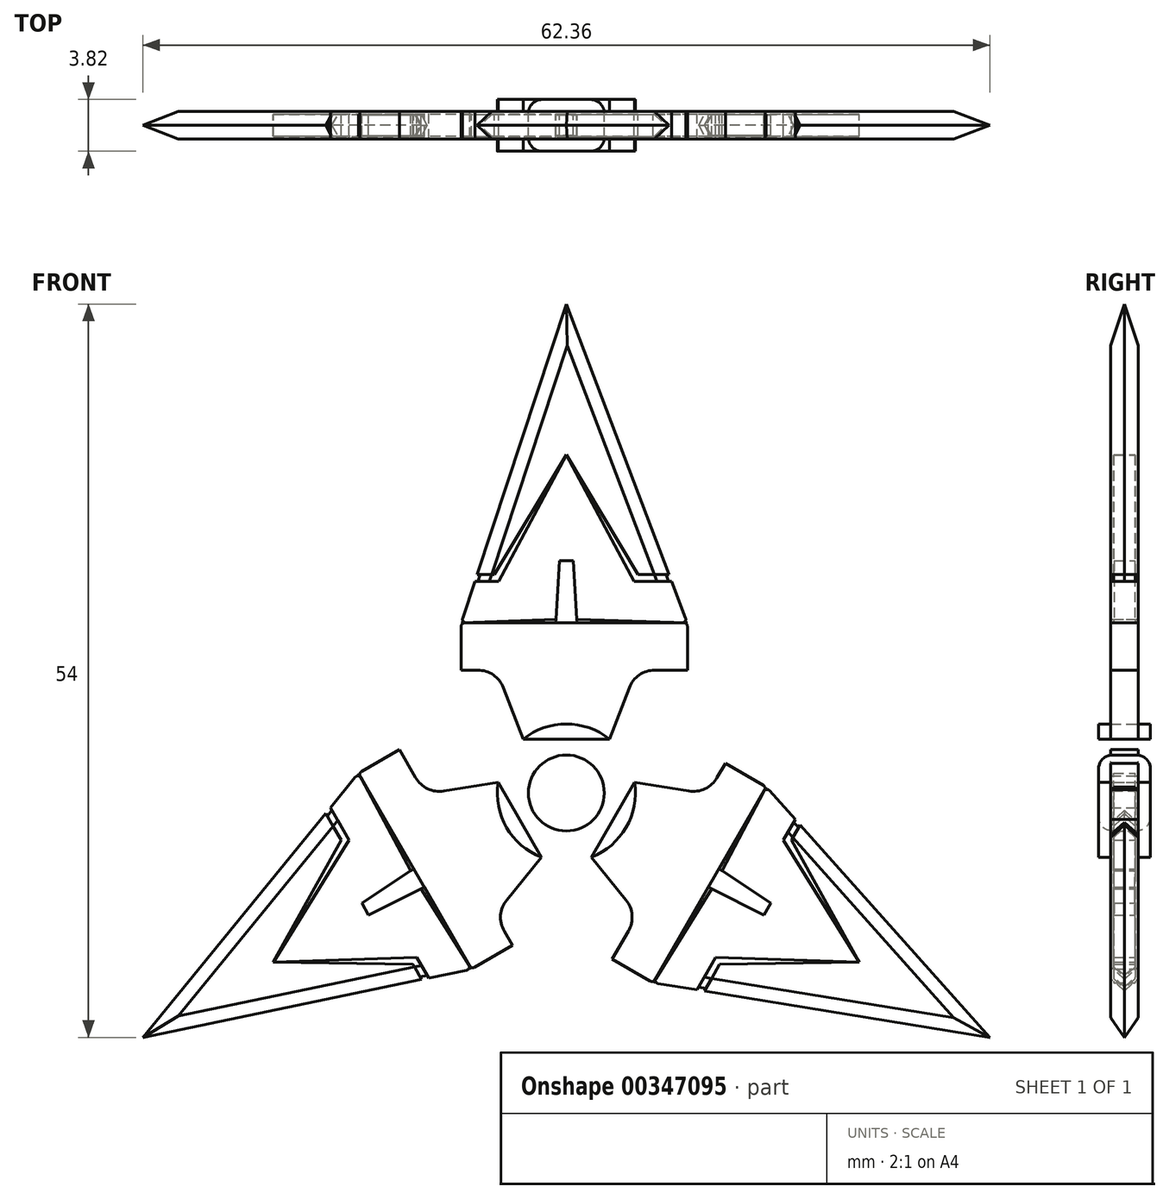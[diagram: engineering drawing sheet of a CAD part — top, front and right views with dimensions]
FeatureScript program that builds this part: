
annotation { "Feature Type Name" : "Feature", "Feature Type Description" : "" }
export const myFeature = defineFeature(function(context is Context, id is Id, definition is map)
    precondition{}
    {
        {
            var Q0;
            Q0=qCreatedBy(makeId("Front.planeOp"),FACE);
            var sketch = newSketch(context, id + "F0", { "sketchPlane" : qUnion([Q0])});
            skCircle(sketch, "E0", {"center": v(0, 0) * mm, "radius": 5.08 * mm});
            skLineSegment(sketch, "E1.bottom", {"start": v(-7.75, 12.52) * mm, "end": v(8.91, 12.52) * mm});
            skLineSegment(sketch, "E1.top", {"start": v(-7.75, 9.04) * mm, "end": v(8.91, 9.04) * mm});
            skLineSegment(sketch, "E1.left", {"start": v(-7.75, 12.52) * mm, "end": v(-7.75, 9.04) * mm});
            skLineSegment(sketch, "E1.right", {"start": v(8.91, 12.52) * mm, "end": v(8.91, 9.04) * mm});
            skLineSegment(sketch, "E2.right", {"start": v(3.18, 9.04) * mm, "end": v(3.18, 3.96) * mm});
            skLineSegment(sketch, "E3.MirrorCS", {"start": v(-3.18, 9.04) * mm, "end": v(-3.18, 3.96) * mm});
            skLineSegment(sketch, "E4", {"start": v(-3.18, 3.96) * mm, "end": v(-5.13, 9.04) * mm});
            skLineSegment(sketch, "E5", {"start": v(3.18, 3.96) * mm, "end": v(5.13, 9.04) * mm});
            skLineSegment(sketch, "E6", {"start": v(-7.75, 12.52) * mm, "end": v(0, 36) * mm});
            skLineSegment(sketch, "E7", {"start": v(8.91, 12.52) * mm, "end": v(0, 36) * mm});
            skLineSegment(sketch, "E8", {"start": v(0, 36) * mm, "end": v(0, 0) * mm});
            skCircle(sketch, "E9.0", {"center": v(0, 0) * mm, "radius": 2.8 * mm});
            skLineSegment(sketch, "E10", {"start": v(-3.18, 3.96) * mm, "end": v(3.18, 3.96) * mm});
            skLineSegment(sketch, "E11.bottom", {"start": v(0.78, 12.52) * mm, "end": v(-0.78, 12.52) * mm});
            skLineSegment(sketch, "E11.top", {"start": v(0.5, 17.1) * mm, "end": v(-0.5, 17.1) * mm});
            skPoint(sketch, "E11.middle", {"position": v(0, 16.34) * mm});
            skLineSegment(sketch, "E12.MirrorCS", {"start": v(0, 24.88) * mm, "end": v(4.98, 15.58) * mm});
            skLineSegment(sketch, "E13.MirrorCS", {"start": v(4.98, 15.58) * mm, "end": v(7.75, 15.58) * mm});
            skLineSegment(sketch, "E14.0", {"start": v(5.29, 16.1) * mm, "end": v(7.56, 16.1) * mm});
            skLineSegment(sketch, "E15", {"start": v(5.29, 16.1) * mm, "end": v(0, 24.9) * mm});
            skLineSegment(sketch, "E16.MirrorCS", {"start": v(-5.29, 16.1) * mm, "end": v(0, 24.9) * mm});
            skLineSegment(sketch, "E17.MirrorCS", {"start": v(0, 24.88) * mm, "end": v(-4.98, 15.58) * mm});
            skLineSegment(sketch, "E18.MirrorCS", {"start": v(-5.29, 16.1) * mm, "end": v(-7.56, 16.1) * mm});
            skLineSegment(sketch, "E19.MirrorCS", {"start": v(-4.98, 15.58) * mm, "end": v(-7.75, 15.58) * mm});
            skLineSegment(sketch, "E20", {"start": v(-0.5, 17.1) * mm, "end": v(-0.78, 12.52) * mm});
            skLineSegment(sketch, "E21", {"start": v(0.5, 17.1) * mm, "end": v(0.78, 12.52) * mm});
            skLineSegment(sketch, "E22", {"start": v(-7.75, 12.52) * mm, "end": v(-0.77, 12.8) * mm});
            skLineSegment(sketch, "E23", {"start": v(0.77, 12.8) * mm, "end": v(8.91, 12.52) * mm});
            skLineSegment(sketch, "E24.1.0", {"start": v(-9.42, -1.77) * mm, "end": v(-5.02, 0.77) * mm});
            skPoint(sketch, "E24.1.1", {"position": v(-14.15, -8.17) * mm});
            skLineSegment(sketch, "E24.1.2", {"start": v(-15.3, 1.45) * mm, "end": v(-12.29, 3.2) * mm});
            skLineSegment(sketch, "E24.1.3", {"start": v(-6.97, -12.97) * mm, "end": v(-15.3, 1.45) * mm});
            skLineSegment(sketch, "E24.1.4", {"start": v(-16.58, -3.47) * mm, "end": v(-21.57, -12.45) * mm});
            skLineSegment(sketch, "E24.1.5", {"start": v(-3.96, -11.23) * mm, "end": v(-12.29, 3.2) * mm});
            skLineSegment(sketch, "E24.1.6", {"start": v(-21.55, -12.44) * mm, "end": v(-11, -12.1) * mm});
            skLineSegment(sketch, "E24.1.7", {"start": v(-11.3, -12.63) * mm, "end": v(-21.57, -12.45) * mm});
            skLineSegment(sketch, "E24.1.8", {"start": v(-1.85, -4.73) * mm, "end": v(-5.02, 0.77) * mm});
            skLineSegment(sketch, "E24.1.9", {"start": v(-11.46, -5.73) * mm, "end": v(-15.3, 1.45) * mm});
            skLineSegment(sketch, "E24.1.10", {"start": v(-5.02, 0.77) * mm, "end": v(-10.4, -0.08) * mm});
            skLineSegment(sketch, "E24.1.11", {"start": v(-6.97, -12.97) * mm, "end": v(-3.96, -11.23) * mm});
            skLineSegment(sketch, "E24.1.12", {"start": v(-6.24, -7.27) * mm, "end": v(-1.85, -4.73) * mm});
            skLineSegment(sketch, "E24.1.13", {"start": v(-6.97, -12.97) * mm, "end": v(-31.18, -18) * mm});
            skLineSegment(sketch, "E24.1.14", {"start": v(-6.97, -12.97) * mm, "end": v(-10.7, -7.06) * mm});
            skLineSegment(sketch, "E24.1.15", {"start": v(-1.85, -4.73) * mm, "end": v(-5.27, -8.96) * mm});
            skLineSegment(sketch, "E24.1.16", {"start": v(-21.55, -12.44) * mm, "end": v(-15.99, -3.47) * mm});
            skLineSegment(sketch, "E24.1.17", {"start": v(-15.3, 1.45) * mm, "end": v(-31.18, -18) * mm});
            skLineSegment(sketch, "E24.1.18", {"start": v(-15.06, -8.11) * mm, "end": v(-11.24, -5.58) * mm});
            skLineSegment(sketch, "E24.1.19", {"start": v(-14.55, -8.98) * mm, "end": v(-10.46, -6.94) * mm});
            skLineSegment(sketch, "E24.1.20", {"start": v(-15.06, -8.11) * mm, "end": v(-14.55, -8.98) * mm});
            skLineSegment(sketch, "E24.1.21", {"start": v(-16.58, -3.47) * mm, "end": v(-17.71, -1.5) * mm});
            skLineSegment(sketch, "E24.1.22", {"start": v(-11.24, -5.58) * mm, "end": v(-10.46, -6.94) * mm});
            skLineSegment(sketch, "E24.1.23", {"start": v(-11, -12.1) * mm, "end": v(-9.62, -14.5) * mm});
            skLineSegment(sketch, "E24.1.24", {"start": v(-15.99, -3.47) * mm, "end": v(-17.37, -1.08) * mm});
            skLineSegment(sketch, "E24.1.25", {"start": v(-11.3, -12.63) * mm, "end": v(-10.16, -14.6) * mm});
            skLineSegment(sketch, "E24.2.0", {"start": v(6.24, -7.27) * mm, "end": v(1.85, -4.73) * mm});
            skPoint(sketch, "E24.2.1", {"position": v(14.15, -8.17) * mm});
            skLineSegment(sketch, "E24.2.2", {"start": v(6.4, -13.98) * mm, "end": v(3.38, -12.24) * mm});
            skLineSegment(sketch, "E24.2.3", {"start": v(14.72, 0.45) * mm, "end": v(6.4, -13.98) * mm});
            skLineSegment(sketch, "E24.2.4", {"start": v(11.3, -12.63) * mm, "end": v(21.57, -12.45) * mm});
            skLineSegment(sketch, "E24.2.5", {"start": v(11.7, 2.19) * mm, "end": v(3.38, -12.24) * mm});
            skLineSegment(sketch, "E24.2.6", {"start": v(21.55, -12.44) * mm, "end": v(15.99, -3.47) * mm});
            skLineSegment(sketch, "E24.2.7", {"start": v(16.58, -3.47) * mm, "end": v(21.57, -12.45) * mm});
            skLineSegment(sketch, "E24.2.8", {"start": v(5.02, 0.77) * mm, "end": v(1.85, -4.73) * mm});
            skLineSegment(sketch, "E24.2.9", {"start": v(10.7, -7.06) * mm, "end": v(6.4, -13.98) * mm});
            skLineSegment(sketch, "E24.2.10", {"start": v(1.85, -4.73) * mm, "end": v(5.27, -8.96) * mm});
            skLineSegment(sketch, "E24.2.11", {"start": v(14.72, 0.45) * mm, "end": v(11.7, 2.19) * mm});
            skLineSegment(sketch, "E24.2.12", {"start": v(9.42, -1.77) * mm, "end": v(5.02, 0.77) * mm});
            skLineSegment(sketch, "E24.2.13", {"start": v(14.72, 0.45) * mm, "end": v(31.18, -18) * mm});
            skLineSegment(sketch, "E24.2.14", {"start": v(14.72, 0.45) * mm, "end": v(11.46, -5.73) * mm});
            skLineSegment(sketch, "E24.2.15", {"start": v(5.02, 0.77) * mm, "end": v(10.4, -0.08) * mm});
            skLineSegment(sketch, "E24.2.16", {"start": v(21.55, -12.44) * mm, "end": v(11, -12.1) * mm});
            skLineSegment(sketch, "E24.2.17", {"start": v(6.4, -13.98) * mm, "end": v(31.18, -18) * mm});
            skLineSegment(sketch, "E24.2.18", {"start": v(14.55, -8.98) * mm, "end": v(10.46, -6.94) * mm});
            skLineSegment(sketch, "E24.2.19", {"start": v(15.06, -8.11) * mm, "end": v(11.24, -5.58) * mm});
            skLineSegment(sketch, "E24.2.20", {"start": v(14.55, -8.98) * mm, "end": v(15.06, -8.11) * mm});
            skLineSegment(sketch, "E24.2.21", {"start": v(11.3, -12.63) * mm, "end": v(10.16, -14.6) * mm});
            skLineSegment(sketch, "E24.2.22", {"start": v(10.46, -6.94) * mm, "end": v(11.24, -5.58) * mm});
            skLineSegment(sketch, "E24.2.23", {"start": v(15.99, -3.47) * mm, "end": v(17.37, -1.08) * mm});
            skLineSegment(sketch, "E24.2.24", {"start": v(11, -12.1) * mm, "end": v(9.62, -14.5) * mm});
            skLineSegment(sketch, "E24.2.25", {"start": v(16.58, -3.47) * mm, "end": v(17.71, -1.5) * mm});
            skSolve(sketch);
        }
        {
            var Q0;
            {var subQ4=sQuery(id+"F0.wireOp",EDGE,"E16.MirrorCS");Q0=makeQuery(id+"F0.imprint","IMPRINT",FACE,{"disambiguationData":[TD([[makeQuery(id+"F0.imprint","IMPRINT",EDGE,{"derivedFrom":subQ4}),1.0]])]});}
            var Q1;
            {var subQ3=sQuery(id+"F0.wireOp",EDGE,"E14.0");Q1=makeQuery(id+"F0.imprint","IMPRINT",FACE,{"disambiguationData":[TD([[makeQuery(id+"F0.imprint","IMPRINT",EDGE,{"derivedFrom":subQ3}),1.0]])]});}
            var Q2;
            {var subQ5=sQuery(id+"F0.wireOp",EDGE,"E17.MirrorCS");Q2=makeQuery(id+"F0.imprint","IMPRINT",FACE,{"disambiguationData":[TD([[makeQuery(id+"F0.imprint","IMPRINT",EDGE,{"derivedFrom":subQ5}),1.0]])]});}
            var Q3;
            {var subQ0=sQuery(id+"F0.wireOp",EDGE,"E12.MirrorCS");Q3=makeQuery(id+"F0.imprint","IMPRINT",FACE,{"disambiguationData":[TD([[makeQuery(id+"F0.imprint","IMPRINT",EDGE,{"derivedFrom":subQ0}),-1.0]])]});}
            var Q4;
            {var subQ0=sQuery(id+"F0.wireOp",EDGE,"E1.right");Q4=makeQuery(id+"F0.imprint","IMPRINT",FACE,{"disambiguationData":[TD([[makeQuery(id+"F0.imprint","IMPRINT",EDGE,{"derivedFrom":subQ0}),-1.0]])]});}
            var Q5;
            {var subQ5=sQuery(id+"F0.wireOp",EDGE,"E1.left");Q5=makeQuery(id+"F0.imprint","IMPRINT",FACE,{"disambiguationData":[TD([[makeQuery(id+"F0.imprint","IMPRINT",EDGE,{"derivedFrom":subQ5}),1.0]])]});}
            var Q6;
            {var subQ0=sQuery(id+"F0.wireOp",EDGE,"E3.MirrorCS");Q6=makeQuery(id+"F0.imprint","IMPRINT",FACE,{"disambiguationData":[TD([[makeQuery(id+"F0.imprint","IMPRINT",EDGE,{"derivedFrom":subQ0}),-1.0]])]});}
            var Q7;
            {var subQ0=sQuery(id+"F0.wireOp",EDGE,"E2.right");Q7=makeQuery(id+"F0.imprint","IMPRINT",FACE,{"disambiguationData":[TD([[makeQuery(id+"F0.imprint","IMPRINT",EDGE,{"derivedFrom":subQ0}),1.0]])]});}
            var Q8;
            {var subQ0=sQuery(id+"F0.wireOp",EDGE,"E2.right");Q8=makeQuery(id+"F0.imprint","IMPRINT",FACE,{"disambiguationData":[TD([[makeQuery(id+"F0.imprint","IMPRINT",EDGE,{"derivedFrom":subQ0}),-1.0]])]});}
            var Q9;
            {var subQ0=sQuery(id+"F0.wireOp",EDGE,"E3.MirrorCS");Q9=makeQuery(id+"F0.imprint","IMPRINT",FACE,{"disambiguationData":[TD([[makeQuery(id+"F0.imprint","IMPRINT",EDGE,{"derivedFrom":subQ0}),1.0]])]});}
            var Q10;
            {var subQ0=sQuery(id+"F0.wireOp",EDGE,"E10");var subQ3=sQuery(id+"F0.wireOp",EDGE,"E8");var subQ5=makeQuery(id+"F0.imprint","INTERSECT",VERTEX,{"derivedFrom":[subQ3,subQ0]});Q10=makeQuery(id+"F0.imprint","IMPRINT",FACE,{"disambiguationData":[TD([[makeQuery(id+"F0.imprint","IMPRINT",EDGE,{"disambiguationData":[TD([[subQ5,1.0]])],"derivedFrom":subQ3}),-1.0]])]});}
            var Q11;
            {var subQ0=sQuery(id+"F0.wireOp",EDGE,"E10");var subQ3=sQuery(id+"F0.wireOp",EDGE,"E8");var subQ5=makeQuery(id+"F0.imprint","INTERSECT",VERTEX,{"derivedFrom":[subQ3,subQ0]});Q11=makeQuery(id+"F0.imprint","IMPRINT",FACE,{"disambiguationData":[TD([[makeQuery(id+"F0.imprint","IMPRINT",EDGE,{"disambiguationData":[TD([[subQ5,1.0]])],"derivedFrom":subQ3}),1.0]])]});}
            var Q12;
            {var subQ0=sQuery(id+"F0.wireOp",EDGE,"E24.2.8");Q12=makeQuery(id+"F0.imprint","IMPRINT",FACE,{"disambiguationData":[TD([[makeQuery(id+"F0.imprint","IMPRINT",EDGE,{"derivedFrom":subQ0}),1.0]])]});}
            var Q13;
            {var subQ0=sQuery(id+"F0.wireOp",EDGE,"E24.1.8");Q13=makeQuery(id+"F0.imprint","IMPRINT",FACE,{"disambiguationData":[TD([[makeQuery(id+"F0.imprint","IMPRINT",EDGE,{"derivedFrom":subQ0}),1.0]])]});}
            var Q14;
            {var subQ4=sQuery(id+"F0.wireOp",EDGE,"E24.2.2");Q14=makeQuery(id+"F0.imprint","IMPRINT",FACE,{"disambiguationData":[TD([[makeQuery(id+"F0.imprint","IMPRINT",EDGE,{"derivedFrom":subQ4}),-1.0]])]});}
            var Q15;
            {var subQ0=sQuery(id+"F0.wireOp",EDGE,"E24.2.12");Q15=makeQuery(id+"F0.imprint","IMPRINT",FACE,{"disambiguationData":[TD([[makeQuery(id+"F0.imprint","IMPRINT",EDGE,{"derivedFrom":subQ0}),-1.0]])]});}
            var Q16;
            {var subQ1=sQuery(id+"F0.wireOp",EDGE,"E24.2.0");Q16=makeQuery(id+"F0.imprint","IMPRINT",FACE,{"disambiguationData":[TD([[makeQuery(id+"F0.imprint","IMPRINT",EDGE,{"derivedFrom":subQ1}),-1.0]])]});}
            var Q17;
            {var subQ0=sQuery(id+"F0.wireOp",EDGE,"E24.2.0");Q17=makeQuery(id+"F0.imprint","IMPRINT",FACE,{"disambiguationData":[TD([[makeQuery(id+"F0.imprint","IMPRINT",EDGE,{"derivedFrom":subQ0}),1.0]])]});}
            var Q18;
            Q18=makeQuery(id+"F0.imprint","IMPRINT",FACE,{"disambiguationData":[TD([[makeQuery(id+"F0.imprint","IMPRINT",EDGE,{"derivedFrom":sQuery(id+"F0.wireOp",EDGE,"E24.2.6")}),1.0]])]});
            var Q19;
            Q19=makeQuery(id+"F0.imprint","IMPRINT",FACE,{"disambiguationData":[TD([[makeQuery(id+"F0.imprint","IMPRINT",EDGE,{"derivedFrom":sQuery(id+"F0.wireOp",EDGE,"E24.2.4")}),-1.0]])]});
            var Q20;
            Q20=makeQuery(id+"F0.imprint","IMPRINT",FACE,{"disambiguationData":[TD([[makeQuery(id+"F0.imprint","IMPRINT",EDGE,{"derivedFrom":sQuery(id+"F0.wireOp",EDGE,"E24.1.4")}),-1.0]])]});
            var Q21;
            Q21=makeQuery(id+"F0.imprint","IMPRINT",FACE,{"disambiguationData":[TD([[makeQuery(id+"F0.imprint","IMPRINT",EDGE,{"derivedFrom":sQuery(id+"F0.wireOp",EDGE,"E24.1.6")}),1.0]])]});
            var Q22;
            {var subQ4=sQuery(id+"F0.wireOp",EDGE,"E24.1.2");Q22=makeQuery(id+"F0.imprint","IMPRINT",FACE,{"disambiguationData":[TD([[makeQuery(id+"F0.imprint","IMPRINT",EDGE,{"derivedFrom":subQ4}),-1.0]])]});}
            var Q23;
            {var subQ0=sQuery(id+"F0.wireOp",EDGE,"E24.1.0");Q23=makeQuery(id+"F0.imprint","IMPRINT",FACE,{"disambiguationData":[TD([[makeQuery(id+"F0.imprint","IMPRINT",EDGE,{"derivedFrom":subQ0}),1.0]])]});}
            var Q24;
            {var subQ1=sQuery(id+"F0.wireOp",EDGE,"E24.1.0");Q24=makeQuery(id+"F0.imprint","IMPRINT",FACE,{"disambiguationData":[TD([[makeQuery(id+"F0.imprint","IMPRINT",EDGE,{"derivedFrom":subQ1}),-1.0]])]});}
            var Q25;
            {var subQ0=sQuery(id+"F0.wireOp",EDGE,"E24.1.12");Q25=makeQuery(id+"F0.imprint","IMPRINT",FACE,{"disambiguationData":[TD([[makeQuery(id+"F0.imprint","IMPRINT",EDGE,{"derivedFrom":subQ0}),-1.0]])]});}
            extrude(context, id + "F1", {"entities" : qUnion([Q0, Q1, Q2, Q3, Q4, Q5, Q6, Q7, Q8, Q9, Q10, Q11, Q12, Q13, Q14, Q15, Q16, Q17, Q18, Q19, Q20, Q21, Q22, Q23, Q24, Q25]), "endBound" : BoundingType.SYMMETRIC, "depth" : 2.03 * mm});
        }
        {
            var Q0;
            {var subQ4=sQuery(id+"F0.wireOp",EDGE,"E24.2.20");Q0=makeQuery(id+"F0.imprint","IMPRINT",FACE,{"disambiguationData":[TD([[makeQuery(id+"F0.imprint","IMPRINT",EDGE,{"derivedFrom":subQ4}),1.0]])]});}
            var Q1;
            {var subQ1=sQuery(id+"F0.wireOp",EDGE,"E11.top");var subQ4=sQuery(id+"F0.wireOp",EDGE,"E8");var subQ5=makeQuery(id+"F0.imprint","INTERSECT",VERTEX,{"derivedFrom":[subQ4,subQ1]});Q1=makeQuery(id+"F0.imprint","IMPRINT",FACE,{"disambiguationData":[TD([[makeQuery(id+"F0.imprint","IMPRINT",EDGE,{"disambiguationData":[TD([[subQ5,-1.0]])],"derivedFrom":subQ4}),1.0]])]});}
            var Q2;
            {var subQ1=sQuery(id+"F0.wireOp",EDGE,"E11.top");var subQ6=sQuery(id+"F0.wireOp",EDGE,"E8");var subQ8=makeQuery(id+"F0.imprint","INTERSECT",VERTEX,{"derivedFrom":[subQ6,subQ1]});Q2=makeQuery(id+"F0.imprint","IMPRINT",FACE,{"disambiguationData":[TD([[makeQuery(id+"F0.imprint","IMPRINT",EDGE,{"disambiguationData":[TD([[subQ8,-1.0]])],"derivedFrom":subQ6}),-1.0]])]});}
            var Q3;
            {var subQ4=sQuery(id+"F0.wireOp",EDGE,"E24.1.20");Q3=makeQuery(id+"F0.imprint","IMPRINT",FACE,{"disambiguationData":[TD([[makeQuery(id+"F0.imprint","IMPRINT",EDGE,{"derivedFrom":subQ4}),1.0]])]});}
            extrude(context, id + "F2", {"entities" : qUnion([Q0, Q1, Q2, Q3]), "endBound" : BoundingType.SYMMETRIC, "depth" : 1.52 * mm});
        }
        {
            var Q0;
            Q0=makeQuery(id+"F0.imprint","IMPRINT",FACE,{"disambiguationData":[TD([[makeQuery(id+"F0.imprint","IMPRINT",EDGE,{"derivedFrom":sQuery(id+"F0.wireOp",EDGE,"E24.1.4")}),1.0]])]});
            var Q1;
            {var subQ0=sQuery(id+"F0.wireOp",EDGE,"E24.1.14");Q1=makeQuery(id+"F0.imprint","IMPRINT",FACE,{"disambiguationData":[TD([[makeQuery(id+"F0.imprint","IMPRINT",EDGE,{"derivedFrom":subQ0}),-1.0]])]});}
            var Q2;
            {var subQ0=sQuery(id+"F0.wireOp",EDGE,"E24.1.9");Q2=makeQuery(id+"F0.imprint","IMPRINT",FACE,{"disambiguationData":[TD([[makeQuery(id+"F0.imprint","IMPRINT",EDGE,{"derivedFrom":subQ0}),-1.0]])]});}
            var Q3;
            Q3=makeQuery(id+"F0.imprint","IMPRINT",FACE,{"disambiguationData":[TD([[makeQuery(id+"F0.imprint","IMPRINT",EDGE,{"derivedFrom":sQuery(id+"F0.wireOp",EDGE,"E24.2.4")}),1.0]])]});
            var Q4;
            {var subQ0=sQuery(id+"F0.wireOp",EDGE,"E24.2.9");Q4=makeQuery(id+"F0.imprint","IMPRINT",FACE,{"disambiguationData":[TD([[makeQuery(id+"F0.imprint","IMPRINT",EDGE,{"derivedFrom":subQ0}),-1.0]])]});}
            var Q5;
            {var subQ0=sQuery(id+"F0.wireOp",EDGE,"E24.2.14");Q5=makeQuery(id+"F0.imprint","IMPRINT",FACE,{"disambiguationData":[TD([[makeQuery(id+"F0.imprint","IMPRINT",EDGE,{"derivedFrom":subQ0}),-1.0]])]});}
            var Q6;
            {var subQ0=sQuery(id+"F0.wireOp",EDGE,"E22");Q6=makeQuery(id+"F0.imprint","IMPRINT",FACE,{"disambiguationData":[TD([[makeQuery(id+"F0.imprint","IMPRINT",EDGE,{"derivedFrom":subQ0}),-1.0]])]});}
            var Q7;
            {var subQ0=sQuery(id+"F0.wireOp",EDGE,"E23");Q7=makeQuery(id+"F0.imprint","IMPRINT",FACE,{"disambiguationData":[TD([[makeQuery(id+"F0.imprint","IMPRINT",EDGE,{"derivedFrom":subQ0}),-1.0]])]});}
            var Q8;
            {var subQ1=sQuery(id+"F0.wireOp",EDGE,"E16.MirrorCS");Q8=makeQuery(id+"F0.imprint","IMPRINT",FACE,{"disambiguationData":[TD([[makeQuery(id+"F0.imprint","IMPRINT",EDGE,{"derivedFrom":subQ1}),-1.0]])]});}
            var Q9;
            {var subQ1=sQuery(id+"F0.wireOp",EDGE,"E12.MirrorCS");Q9=makeQuery(id+"F0.imprint","IMPRINT",FACE,{"disambiguationData":[TD([[makeQuery(id+"F0.imprint","IMPRINT",EDGE,{"derivedFrom":subQ1}),1.0]])]});}
            extrude(context, id + "F3", {"entities" : qUnion([Q0, Q1, Q2, Q3, Q4, Q5, Q6, Q7, Q8, Q9]), "endBound" : BoundingType.SYMMETRIC, "depth" : 1.6 * mm});
        }
        {
            var Q0;
            Q0=makeQuery(id+"F1.opExtrude","SWEPT_EDGE",EDGE,{"disambiguationData":[OSD([sQuery(id+"F0.wireOp",EDGE,"E1.top"),sQuery(id+"F0.wireOp",EDGE,"E4")])]});
            var Q1;
            Q1=makeQuery(id+"F1.opExtrude","SWEPT_EDGE",EDGE,{"disambiguationData":[OSD([sQuery(id+"F0.wireOp",EDGE,"E1.top"),sQuery(id+"F0.wireOp",EDGE,"E5")])]});
            var Q2;
            Q2=makeQuery(id+"F1.opExtrude","SWEPT_EDGE",EDGE,{"disambiguationData":[OSD([sQuery(id+"F0.wireOp",EDGE,"E24.2.5"),sQuery(id+"F0.wireOp",EDGE,"E24.2.15")])]});
            var Q3;
            Q3=makeQuery(id+"F1.opExtrude","SWEPT_EDGE",EDGE,{"disambiguationData":[OSD([sQuery(id+"F0.wireOp",EDGE,"E24.1.5"),sQuery(id+"F0.wireOp",EDGE,"E24.1.10")])]});
            var Q4;
            Q4=makeQuery(id+"F1.opExtrude","SWEPT_EDGE",EDGE,{"disambiguationData":[OSD([sQuery(id+"F0.wireOp",EDGE,"E24.1.5"),sQuery(id+"F0.wireOp",EDGE,"E24.1.15")])]});
            var Q5;
            Q5=makeQuery(id+"F1.opExtrude","SWEPT_EDGE",EDGE,{"disambiguationData":[OSD([sQuery(id+"F0.wireOp",EDGE,"E24.2.5"),sQuery(id+"F0.wireOp",EDGE,"E24.2.10")])]});
            fillet(context, id + "F4", {"entities" : qUnion([Q0, Q1, Q2, Q3, Q4, Q5]), "radius" : 2.03 * mm, "tangentPropagation" : true, "allowEdgeOverflow" : false});
        }
        {
            var Q0;
            {var subQ0=sQuery(id+"F0.wireOp",EDGE,"E1.bottom");Q0=makeQuery(id+"F1.opExtrude","SWEPT_EDGE",EDGE,{"disambiguationData":[OSD([sQuery(id+"F0.wireOp",EDGE,"E24.1.2"),sQuery(id+"F0.wireOp",EDGE,"E24.1.3"),sQuery(id+"F0.wireOp",EDGE,"E24.1.9"),sQuery(id+"F0.wireOp",EDGE,"E24.1.17")]),ownerDisambiguation([makeQuery(id+"F0.imprint","IMPRINT",EDGE,{"disambiguationData":[TD([[makeQuery(id+"F0.imprint","INTERSECT",VERTEX,{"derivedFrom":[subQ0,sQuery(id+"F0.wireOp",EDGE,"E11.bottom"),sQuery(id+"F0.wireOp",EDGE,"E20")]}),1.0]])],"derivedFrom":subQ0})])]});}
            var Q1;
            {var subQ0=sQuery(id+"F0.wireOp",EDGE,"E1.bottom");Q1=makeQuery(id+"F1.opExtrude","SWEPT_EDGE",EDGE,{"disambiguationData":[OSD([sQuery(id+"F0.wireOp",EDGE,"E24.1.3"),sQuery(id+"F0.wireOp",EDGE,"E24.1.11"),sQuery(id+"F0.wireOp",EDGE,"E24.1.13"),sQuery(id+"F0.wireOp",EDGE,"E24.1.14")]),ownerDisambiguation([makeQuery(id+"F0.imprint","IMPRINT",EDGE,{"disambiguationData":[TD([[makeQuery(id+"F0.imprint","INTERSECT",VERTEX,{"derivedFrom":[subQ0,sQuery(id+"F0.wireOp",EDGE,"E11.bottom"),sQuery(id+"F0.wireOp",EDGE,"E20")]}),1.0]])],"derivedFrom":subQ0})])]});}
            var Q2;
            {var subQ0=sQuery(id+"F0.wireOp",EDGE,"E1.bottom");Q2=makeQuery(id+"F1.opExtrude","SWEPT_EDGE",EDGE,{"disambiguationData":[OSD([sQuery(id+"F0.wireOp",EDGE,"E24.2.2"),sQuery(id+"F0.wireOp",EDGE,"E24.2.3"),sQuery(id+"F0.wireOp",EDGE,"E24.2.9"),sQuery(id+"F0.wireOp",EDGE,"E24.2.17")]),ownerDisambiguation([makeQuery(id+"F0.imprint","IMPRINT",EDGE,{"disambiguationData":[TD([[makeQuery(id+"F0.imprint","INTERSECT",VERTEX,{"derivedFrom":[subQ0,sQuery(id+"F0.wireOp",EDGE,"E11.bottom"),sQuery(id+"F0.wireOp",EDGE,"E20")]}),1.0]])],"derivedFrom":subQ0})])]});}
            var Q3;
            {var subQ0=sQuery(id+"F0.wireOp",EDGE,"E1.bottom");Q3=makeQuery(id+"F1.opExtrude","SWEPT_EDGE",EDGE,{"disambiguationData":[OSD([sQuery(id+"F0.wireOp",EDGE,"E24.2.3"),sQuery(id+"F0.wireOp",EDGE,"E24.2.11"),sQuery(id+"F0.wireOp",EDGE,"E24.2.13"),sQuery(id+"F0.wireOp",EDGE,"E24.2.14")]),ownerDisambiguation([makeQuery(id+"F0.imprint","IMPRINT",EDGE,{"disambiguationData":[TD([[makeQuery(id+"F0.imprint","INTERSECT",VERTEX,{"derivedFrom":[subQ0,sQuery(id+"F0.wireOp",EDGE,"E11.bottom"),sQuery(id+"F0.wireOp",EDGE,"E20")]}),1.0]])],"derivedFrom":subQ0})])]});}
            var Q4;
            {var subQ0=sQuery(id+"F0.wireOp",EDGE,"E1.bottom");Q4=makeQuery(id+"F1.opExtrude","SWEPT_EDGE",EDGE,{"disambiguationData":[OSD([subQ0,sQuery(id+"F0.wireOp",EDGE,"E1.right"),sQuery(id+"F0.wireOp",EDGE,"E7"),sQuery(id+"F0.wireOp",EDGE,"E23")]),ownerDisambiguation([makeQuery(id+"F0.imprint","IMPRINT",EDGE,{"disambiguationData":[TD([[makeQuery(id+"F0.imprint","INTERSECT",VERTEX,{"derivedFrom":[subQ0,sQuery(id+"F0.wireOp",EDGE,"E11.bottom"),sQuery(id+"F0.wireOp",EDGE,"E20")]}),1.0]])],"derivedFrom":subQ0})])]});}
            var Q5;
            {var subQ0=sQuery(id+"F0.wireOp",EDGE,"E22");var subQ1=sQuery(id+"F0.wireOp",EDGE,"E6");var subQ2=sQuery(id+"F0.wireOp",EDGE,"E1.left");var subQ3=sQuery(id+"F0.wireOp",EDGE,"E1.bottom");Q5=makeQuery(id+"F1.opExtrude","SWEPT_EDGE",EDGE,{"disambiguationData":[OSD([subQ3,subQ2,subQ1,subQ0]),ownerDisambiguation([makeQuery(id+"F0.imprint","IMPRINT",EDGE,{"disambiguationData":[TD([[makeQuery(id+"F0.imprint","INTERSECT",VERTEX,{"derivedFrom":[subQ3,sQuery(id+"F0.wireOp",EDGE,"E11.bottom"),sQuery(id+"F0.wireOp",EDGE,"E20")]}),1.0]])],"derivedFrom":subQ3})])]});}
            fillet(context, id + "F5", {"entities" : qUnion([Q0, Q1, Q2, Q3, Q4, Q5]), "radius" : 0.25 * mm, "tangentPropagation" : true, "allowEdgeOverflow" : false});
        }
        {
            var Q0;
            Q0=makeQuery(id+"F0.imprint","IMPRINT",FACE,{"disambiguationData":[TD([[makeQuery(id+"F0.imprint","IMPRINT",EDGE,{"derivedFrom":sQuery(id+"F0.wireOp",EDGE,"E9.0")}),1.0]])]});
            var Q1;
            {var subQ0=sQuery(id+"F0.wireOp",EDGE,"E24.1.8");Q1=makeQuery(id+"F0.imprint","IMPRINT",FACE,{"disambiguationData":[TD([[makeQuery(id+"F0.imprint","IMPRINT",EDGE,{"derivedFrom":subQ0}),1.0]])]});}
            var Q2;
            {var subQ0=sQuery(id+"F0.wireOp",EDGE,"E24.2.8");Q2=makeQuery(id+"F0.imprint","IMPRINT",FACE,{"disambiguationData":[TD([[makeQuery(id+"F0.imprint","IMPRINT",EDGE,{"derivedFrom":subQ0}),1.0]])]});}
            var Q3;
            {var subQ0=sQuery(id+"F0.wireOp",EDGE,"E10");var subQ3=sQuery(id+"F0.wireOp",EDGE,"E8");var subQ5=makeQuery(id+"F0.imprint","INTERSECT",VERTEX,{"derivedFrom":[subQ3,subQ0]});Q3=makeQuery(id+"F0.imprint","IMPRINT",FACE,{"disambiguationData":[TD([[makeQuery(id+"F0.imprint","IMPRINT",EDGE,{"disambiguationData":[TD([[subQ5,1.0]])],"derivedFrom":subQ3}),1.0]])]});}
            var Q4;
            {var subQ0=sQuery(id+"F0.wireOp",EDGE,"E10");var subQ3=sQuery(id+"F0.wireOp",EDGE,"E8");var subQ5=makeQuery(id+"F0.imprint","INTERSECT",VERTEX,{"derivedFrom":[subQ3,subQ0]});Q4=makeQuery(id+"F0.imprint","IMPRINT",FACE,{"disambiguationData":[TD([[makeQuery(id+"F0.imprint","IMPRINT",EDGE,{"disambiguationData":[TD([[subQ5,1.0]])],"derivedFrom":subQ3}),-1.0]])]});}
            extrude(context, id + "F6", {"entities" : qUnion([Q0, Q1, Q2, Q3, Q4]), "endBound" : BoundingType.SYMMETRIC, "depth" : 3.8 * mm});
        }
        {
            var Q0;
            Q0=makeQuery(id+"F6.opExtrude","CAP_EDGE",EDGE,{"disambiguationData":[OSD([sQuery(id+"F0.wireOp",EDGE,"E0")])],"isStart":true});
            var Q1;
            Q1=makeQuery(id+"F6.opExtrude","CAP_EDGE",EDGE,{"disambiguationData":[OSD([sQuery(id+"F0.wireOp",EDGE,"E9.0")])],"isStart":true});
            var Q2;
            Q2=makeQuery(id+"F6.opExtrude","CAP_EDGE",EDGE,{"disambiguationData":[OSD([sQuery(id+"F0.wireOp",EDGE,"E0")])],"isStart":false});
            var Q3;
            Q3=makeQuery(id+"F6.opExtrude","CAP_EDGE",EDGE,{"disambiguationData":[OSD([sQuery(id+"F0.wireOp",EDGE,"E9.0")])],"isStart":false});
            fillet(context, id + "F7", {"entities" : qUnion([Q0, Q1, Q2, Q3]), "radius" : 1.02 * mm, "tangentPropagation" : true, "allowEdgeOverflow" : false});
        }
        {
            var Q0;
            {var subQ0=sQuery(id+"F0.wireOp",EDGE,"E24.2.17");Q0=makeQuery(id+"F1.opExtrude","CAP_EDGE",EDGE,{"disambiguationData":[OSD([subQ0]),TDD([makeQuery(id+"F0.imprint","IMPRINT",EDGE,{"disambiguationData":[TD([[makeQuery(id+"F0.imprint","INTERSECT",VERTEX,{"derivedFrom":[sQuery(id+"F0.wireOp",EDGE,"E24.2.13"),subQ0]}),1.0]])],"derivedFrom":subQ0})])],"isStart":false});}
            var Q1;
            {var subQ0=sQuery(id+"F0.wireOp",EDGE,"E24.2.17");Q1=makeQuery(id+"F1.opExtrude","CAP_EDGE",EDGE,{"disambiguationData":[OSD([subQ0]),TDD([makeQuery(id+"F0.imprint","IMPRINT",EDGE,{"disambiguationData":[TD([[makeQuery(id+"F0.imprint","INTERSECT",VERTEX,{"derivedFrom":[sQuery(id+"F0.wireOp",EDGE,"E24.2.13"),subQ0]}),1.0]])],"derivedFrom":subQ0})])],"isStart":true});}
            var Q2;
            {var subQ0=sQuery(id+"F0.wireOp",EDGE,"E24.2.13");Q2=makeQuery(id+"F1.opExtrude","CAP_EDGE",EDGE,{"disambiguationData":[OSD([subQ0]),TDD([makeQuery(id+"F0.imprint","IMPRINT",EDGE,{"disambiguationData":[TD([[makeQuery(id+"F0.imprint","INTERSECT",VERTEX,{"derivedFrom":[subQ0,sQuery(id+"F0.wireOp",EDGE,"E24.2.17")]}),1.0]])],"derivedFrom":subQ0})])],"isStart":false});}
            var Q3;
            {var subQ0=sQuery(id+"F0.wireOp",EDGE,"E24.2.13");Q3=makeQuery(id+"F1.opExtrude","CAP_EDGE",EDGE,{"disambiguationData":[OSD([subQ0]),TDD([makeQuery(id+"F0.imprint","IMPRINT",EDGE,{"disambiguationData":[TD([[makeQuery(id+"F0.imprint","INTERSECT",VERTEX,{"derivedFrom":[subQ0,sQuery(id+"F0.wireOp",EDGE,"E24.2.17")]}),1.0]])],"derivedFrom":subQ0})])],"isStart":true});}
            var Q4;
            {var subQ0=sQuery(id+"F0.wireOp",EDGE,"E7");Q4=makeQuery(id+"F1.opExtrude","CAP_EDGE",EDGE,{"disambiguationData":[OSD([subQ0]),TDD([makeQuery(id+"F0.imprint","IMPRINT",EDGE,{"disambiguationData":[TD([[makeQuery(id+"F0.imprint","INTERSECT",VERTEX,{"derivedFrom":[subQ0,sQuery(id+"F0.wireOp",EDGE,"E14.0")]}),-1.0]])],"derivedFrom":subQ0})])],"isStart":true});}
            var Q5;
            {var subQ0=sQuery(id+"F0.wireOp",EDGE,"E7");Q5=makeQuery(id+"F1.opExtrude","CAP_EDGE",EDGE,{"disambiguationData":[OSD([subQ0]),TDD([makeQuery(id+"F0.imprint","IMPRINT",EDGE,{"disambiguationData":[TD([[makeQuery(id+"F0.imprint","INTERSECT",VERTEX,{"derivedFrom":[subQ0,sQuery(id+"F0.wireOp",EDGE,"E14.0")]}),-1.0]])],"derivedFrom":subQ0})])],"isStart":false});}
            var Q6;
            {var subQ0=sQuery(id+"F0.wireOp",EDGE,"E6");Q6=makeQuery(id+"F1.opExtrude","CAP_EDGE",EDGE,{"disambiguationData":[OSD([subQ0]),TDD([makeQuery(id+"F0.imprint","IMPRINT",EDGE,{"disambiguationData":[TD([[makeQuery(id+"F0.imprint","INTERSECT",VERTEX,{"derivedFrom":[subQ0,sQuery(id+"F0.wireOp",EDGE,"E18.MirrorCS")]}),-1.0]])],"derivedFrom":subQ0})])],"isStart":false});}
            var Q7;
            {var subQ0=sQuery(id+"F0.wireOp",EDGE,"E6");Q7=makeQuery(id+"F1.opExtrude","CAP_EDGE",EDGE,{"disambiguationData":[OSD([subQ0]),TDD([makeQuery(id+"F0.imprint","IMPRINT",EDGE,{"disambiguationData":[TD([[makeQuery(id+"F0.imprint","INTERSECT",VERTEX,{"derivedFrom":[subQ0,sQuery(id+"F0.wireOp",EDGE,"E18.MirrorCS")]}),-1.0]])],"derivedFrom":subQ0})])],"isStart":true});}
            var Q8;
            {var subQ0=sQuery(id+"F0.wireOp",EDGE,"E24.1.17");Q8=makeQuery(id+"F1.opExtrude","CAP_EDGE",EDGE,{"disambiguationData":[OSD([subQ0]),TDD([makeQuery(id+"F0.imprint","IMPRINT",EDGE,{"disambiguationData":[TD([[makeQuery(id+"F0.imprint","INTERSECT",VERTEX,{"derivedFrom":[sQuery(id+"F0.wireOp",EDGE,"E24.1.13"),subQ0]}),1.0]])],"derivedFrom":subQ0})])],"isStart":false});}
            var Q9;
            {var subQ0=sQuery(id+"F0.wireOp",EDGE,"E24.1.17");Q9=makeQuery(id+"F1.opExtrude","CAP_EDGE",EDGE,{"disambiguationData":[OSD([subQ0]),TDD([makeQuery(id+"F0.imprint","IMPRINT",EDGE,{"disambiguationData":[TD([[makeQuery(id+"F0.imprint","INTERSECT",VERTEX,{"derivedFrom":[sQuery(id+"F0.wireOp",EDGE,"E24.1.13"),subQ0]}),1.0]])],"derivedFrom":subQ0})])],"isStart":true});}
            var Q10;
            {var subQ0=sQuery(id+"F0.wireOp",EDGE,"E24.1.13");Q10=makeQuery(id+"F1.opExtrude","CAP_EDGE",EDGE,{"disambiguationData":[OSD([subQ0]),TDD([makeQuery(id+"F0.imprint","IMPRINT",EDGE,{"disambiguationData":[TD([[makeQuery(id+"F0.imprint","INTERSECT",VERTEX,{"derivedFrom":[subQ0,sQuery(id+"F0.wireOp",EDGE,"E24.1.17")]}),1.0]])],"derivedFrom":subQ0})])],"isStart":true});}
            var Q11;
            {var subQ0=sQuery(id+"F0.wireOp",EDGE,"E24.1.13");Q11=makeQuery(id+"F1.opExtrude","CAP_EDGE",EDGE,{"disambiguationData":[OSD([subQ0]),TDD([makeQuery(id+"F0.imprint","IMPRINT",EDGE,{"disambiguationData":[TD([[makeQuery(id+"F0.imprint","INTERSECT",VERTEX,{"derivedFrom":[subQ0,sQuery(id+"F0.wireOp",EDGE,"E24.1.17")]}),1.0]])],"derivedFrom":subQ0})])],"isStart":false});}
            var Q12;
            Q12=makeQuery(id+"F3.opExtrude","CAP_EDGE",EDGE,{"disambiguationData":[OSD([sQuery(id+"F0.wireOp",EDGE,"E24.2.13")])],"isStart":true});
            var Q13;
            Q13=makeQuery(id+"F3.opExtrude","CAP_EDGE",EDGE,{"disambiguationData":[OSD([sQuery(id+"F0.wireOp",EDGE,"E24.2.13")])],"isStart":false});
            var Q14;
            {var subQ0=sQuery(id+"F0.wireOp",EDGE,"E24.2.13");Q14=makeQuery(id+"F1.opExtrude","CAP_EDGE",EDGE,{"disambiguationData":[OSD([subQ0]),TDD([makeQuery(id+"F0.imprint","IMPRINT",EDGE,{"disambiguationData":[TD([[makeQuery(id+"F0.imprint","INTERSECT",VERTEX,{"derivedFrom":[subQ0,sQuery(id+"F0.wireOp",EDGE,"E24.2.23")]}),1.0]])],"derivedFrom":subQ0})])],"isStart":false});}
            var Q15;
            {var subQ0=sQuery(id+"F0.wireOp",EDGE,"E24.2.13");Q15=makeQuery(id+"F1.opExtrude","CAP_EDGE",EDGE,{"disambiguationData":[OSD([subQ0]),TDD([makeQuery(id+"F0.imprint","IMPRINT",EDGE,{"disambiguationData":[TD([[makeQuery(id+"F0.imprint","INTERSECT",VERTEX,{"derivedFrom":[subQ0,sQuery(id+"F0.wireOp",EDGE,"E24.2.23")]}),1.0]])],"derivedFrom":subQ0})])],"isStart":true});}
            var Q16;
            Q16=makeQuery(id+"F3.opExtrude","CAP_EDGE",EDGE,{"disambiguationData":[OSD([sQuery(id+"F0.wireOp",EDGE,"E24.2.17")])],"isStart":true});
            var Q17;
            Q17=makeQuery(id+"F3.opExtrude","CAP_EDGE",EDGE,{"disambiguationData":[OSD([sQuery(id+"F0.wireOp",EDGE,"E24.2.17")])],"isStart":false});
            var Q18;
            {var subQ0=sQuery(id+"F0.wireOp",EDGE,"E24.2.17");Q18=makeQuery(id+"F1.opExtrude","CAP_EDGE",EDGE,{"disambiguationData":[OSD([subQ0]),TDD([makeQuery(id+"F0.imprint","IMPRINT",EDGE,{"disambiguationData":[TD([[makeQuery(id+"F0.imprint","INTERSECT",VERTEX,{"derivedFrom":[subQ0,sQuery(id+"F0.wireOp",EDGE,"E24.2.24")]}),1.0]])],"derivedFrom":subQ0})])],"isStart":false});}
            var Q19;
            {var subQ0=sQuery(id+"F0.wireOp",EDGE,"E24.2.17");Q19=makeQuery(id+"F1.opExtrude","CAP_EDGE",EDGE,{"disambiguationData":[OSD([subQ0]),TDD([makeQuery(id+"F0.imprint","IMPRINT",EDGE,{"disambiguationData":[TD([[makeQuery(id+"F0.imprint","INTERSECT",VERTEX,{"derivedFrom":[subQ0,sQuery(id+"F0.wireOp",EDGE,"E24.2.24")]}),1.0]])],"derivedFrom":subQ0})])],"isStart":true});}
            var Q20;
            Q20=makeQuery(id+"F3.opExtrude","CAP_EDGE",EDGE,{"disambiguationData":[OSD([sQuery(id+"F0.wireOp",EDGE,"E7")])],"isStart":true});
            var Q21;
            Q21=makeQuery(id+"F3.opExtrude","CAP_EDGE",EDGE,{"disambiguationData":[OSD([sQuery(id+"F0.wireOp",EDGE,"E7")])],"isStart":false});
            var Q22;
            {var subQ0=sQuery(id+"F0.wireOp",EDGE,"E7");Q22=makeQuery(id+"F1.opExtrude","CAP_EDGE",EDGE,{"disambiguationData":[OSD([subQ0]),TDD([makeQuery(id+"F0.imprint","IMPRINT",EDGE,{"disambiguationData":[TD([[makeQuery(id+"F0.imprint","INTERSECT",VERTEX,{"derivedFrom":[subQ0,sQuery(id+"F0.wireOp",EDGE,"E13.MirrorCS")]}),1.0]])],"derivedFrom":subQ0})])],"isStart":false});}
            var Q23;
            {var subQ0=sQuery(id+"F0.wireOp",EDGE,"E7");Q23=makeQuery(id+"F1.opExtrude","CAP_EDGE",EDGE,{"disambiguationData":[OSD([subQ0]),TDD([makeQuery(id+"F0.imprint","IMPRINT",EDGE,{"disambiguationData":[TD([[makeQuery(id+"F0.imprint","INTERSECT",VERTEX,{"derivedFrom":[subQ0,sQuery(id+"F0.wireOp",EDGE,"E13.MirrorCS")]}),1.0]])],"derivedFrom":subQ0})])],"isStart":true});}
            var Q24;
            Q24=makeQuery(id+"F3.opExtrude","CAP_EDGE",EDGE,{"disambiguationData":[OSD([sQuery(id+"F0.wireOp",EDGE,"E6")])],"isStart":true});
            var Q25;
            Q25=makeQuery(id+"F3.opExtrude","CAP_EDGE",EDGE,{"disambiguationData":[OSD([sQuery(id+"F0.wireOp",EDGE,"E6")])],"isStart":false});
            var Q26;
            {var subQ0=sQuery(id+"F0.wireOp",EDGE,"E6");Q26=makeQuery(id+"F1.opExtrude","CAP_EDGE",EDGE,{"disambiguationData":[OSD([subQ0]),TDD([makeQuery(id+"F0.imprint","IMPRINT",EDGE,{"disambiguationData":[TD([[makeQuery(id+"F0.imprint","INTERSECT",VERTEX,{"derivedFrom":[subQ0,sQuery(id+"F0.wireOp",EDGE,"E19.MirrorCS")]}),1.0]])],"derivedFrom":subQ0})])],"isStart":false});}
            var Q27;
            {var subQ0=sQuery(id+"F0.wireOp",EDGE,"E6");Q27=makeQuery(id+"F1.opExtrude","CAP_EDGE",EDGE,{"disambiguationData":[OSD([subQ0]),TDD([makeQuery(id+"F0.imprint","IMPRINT",EDGE,{"disambiguationData":[TD([[makeQuery(id+"F0.imprint","INTERSECT",VERTEX,{"derivedFrom":[subQ0,sQuery(id+"F0.wireOp",EDGE,"E19.MirrorCS")]}),1.0]])],"derivedFrom":subQ0})])],"isStart":true});}
            var Q28;
            Q28=makeQuery(id+"F3.opExtrude","CAP_EDGE",EDGE,{"disambiguationData":[OSD([sQuery(id+"F0.wireOp",EDGE,"E24.1.17")])],"isStart":false});
            var Q29;
            Q29=makeQuery(id+"F3.opExtrude","CAP_EDGE",EDGE,{"disambiguationData":[OSD([sQuery(id+"F0.wireOp",EDGE,"E24.1.17")])],"isStart":true});
            var Q30;
            {var subQ0=sQuery(id+"F0.wireOp",EDGE,"E24.1.17");Q30=makeQuery(id+"F1.opExtrude","CAP_EDGE",EDGE,{"disambiguationData":[OSD([subQ0]),TDD([makeQuery(id+"F0.imprint","IMPRINT",EDGE,{"disambiguationData":[TD([[makeQuery(id+"F0.imprint","INTERSECT",VERTEX,{"derivedFrom":[subQ0,sQuery(id+"F0.wireOp",EDGE,"E24.1.24")]}),1.0]])],"derivedFrom":subQ0})])],"isStart":true});}
            var Q31;
            {var subQ0=sQuery(id+"F0.wireOp",EDGE,"E24.1.17");Q31=makeQuery(id+"F1.opExtrude","CAP_EDGE",EDGE,{"disambiguationData":[OSD([subQ0]),TDD([makeQuery(id+"F0.imprint","IMPRINT",EDGE,{"disambiguationData":[TD([[makeQuery(id+"F0.imprint","INTERSECT",VERTEX,{"derivedFrom":[subQ0,sQuery(id+"F0.wireOp",EDGE,"E24.1.24")]}),1.0]])],"derivedFrom":subQ0})])],"isStart":false});}
            var Q32;
            Q32=makeQuery(id+"F3.opExtrude","CAP_EDGE",EDGE,{"disambiguationData":[OSD([sQuery(id+"F0.wireOp",EDGE,"E24.1.13")])],"isStart":false});
            var Q33;
            Q33=makeQuery(id+"F3.opExtrude","CAP_EDGE",EDGE,{"disambiguationData":[OSD([sQuery(id+"F0.wireOp",EDGE,"E24.1.13")])],"isStart":true});
            var Q34;
            {var subQ0=sQuery(id+"F0.wireOp",EDGE,"E24.1.13");Q34=makeQuery(id+"F1.opExtrude","CAP_EDGE",EDGE,{"disambiguationData":[OSD([subQ0]),TDD([makeQuery(id+"F0.imprint","IMPRINT",EDGE,{"disambiguationData":[TD([[makeQuery(id+"F0.imprint","INTERSECT",VERTEX,{"derivedFrom":[subQ0,sQuery(id+"F0.wireOp",EDGE,"E24.1.23")]}),1.0]])],"derivedFrom":subQ0})])],"isStart":false});}
            var Q35;
            {var subQ0=sQuery(id+"F0.wireOp",EDGE,"E24.1.13");Q35=makeQuery(id+"F1.opExtrude","CAP_EDGE",EDGE,{"disambiguationData":[OSD([subQ0]),TDD([makeQuery(id+"F0.imprint","IMPRINT",EDGE,{"disambiguationData":[TD([[makeQuery(id+"F0.imprint","INTERSECT",VERTEX,{"derivedFrom":[subQ0,sQuery(id+"F0.wireOp",EDGE,"E24.1.23")]}),1.0]])],"derivedFrom":subQ0})])],"isStart":true});}
            chamfer(context, id + "F8", {"entities" : qUnion([Q0, Q1, Q2, Q3, Q4, Q5, Q6, Q7, Q8, Q9, Q10, Q11, Q12, Q13, Q14, Q15, Q16, Q17, Q18, Q19, Q20, Q21, Q22, Q23, Q24, Q25, Q26, Q27, Q28, Q29, Q30, Q31, Q32, Q33, Q34, Q35]), "width" : 1.02 * mm, "tangentPropagation" : true});
        }
    });
